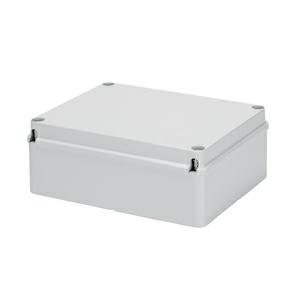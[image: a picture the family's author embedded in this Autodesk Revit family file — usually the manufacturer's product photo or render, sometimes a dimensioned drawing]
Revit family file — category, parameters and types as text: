
# Revit family: Building-ContenitoriParete-GEWISS-44CE-CASSETTE-DERIVAZIONE-PARETE
name_source: partatom
category: Apparecchi elettrici
revit_build: Autodesk Revit 2016 (Build: 20161004_0715(x64)
units: mm (PartAtom-declared; Revit-internal decimal feet)

## family parameters
Condiviso = No
Host = Superficie
Mantenere orientamento annotazione = Sì
Numero OmniClass = 23.80.30.14.24
Punto di calcolo locali = Sì
Quota connettore circolare = Usa diametro
Taglio con vuoti quando caricato = No
Tipo di parte = Normale
Titolo OmniClass = Junction Boxes

## types (1)
- Building-ContenitoriParete-GEWISS-44CE-CASSETTE-DERIVAZIONE-PARETE
    Accessori per ripristino isolamento = GW44621
    Applicazione = Impieghi industriali
    Carico apparente = 0 VA
    Catalogo = BUILDING
    Catalogo Serie = 44 CE
    Classe isolamento = II (secondo Norma IEC 61140)
    Classificazione = Other
    Codice EAN = 8011564014145
    Codice Electrocod = 0231
    Colore = Grigio RAL 7035
    Colore coperchio = Trasparente
    Coperchio = Basso a vite
    Coperchio_ = GEWISS COPERCHIO TRASPARENTE
    Coppia serraggio viti = 1,8NM
    Descrizione = CASSETTA IP56 AR.COP.TRASP.460X380X120
    Dettaglio = Eemento di dettaglio - 44CE : 460x380x120
    Dim. interne BxHxP (mm) = 460x380x120
    Glow Wire Test = 650°C
    Grado di protezione = IP56
    IDF = 5374820f-a702-40f6-8e03-a2dac9afe598
    IDT = 9d7720fb-e677-4d26-8d25-fa01e92eaf96
    Immagine tipo = GW44431.jpg
    Larghezza_interna = 460 mm  [stored 1.50919 ft]
    Lunghezza_interna = 380 mm
    Materiale = Tecnopolimero GWPLAST 120
    Modello = GW44431
    Pareti = Lisce
    Produttore = GEWISS S.p.A.
    Prospetto di default = 1219 mm
    Resistenza agli urti = IK08
    SEO = Cassetta
    Scatola_ = GW - Grigio RAL 7035
    Scheda Tecnica = https://www.gewiss.com
    Spessore = 120 mm  [stored 0.393701 ft]
    Temperatura di impiego = -25 +60 °C
    Termopressione con biglia = 110 °C
    Tipo Materiale = Halogen free secondo norma EN 60754-2
    URL = https://www.gewiss.com
    Versione file RFA = 18.0
    Viti coperchio (n. e Tipo) = 6 isol. a cerniera piombabili
    Voltaggio = 0 V
    Ã˜ max fori eseguibili = 48MM

note: [stored X ft] marks values corroborated as IEEE doubles in the binary element streams (Revit-internal decimal feet)

## geometry (parser evidence)
native form markers: Blend x4, Sweep x2
no freeform markers — native parametric forms only
